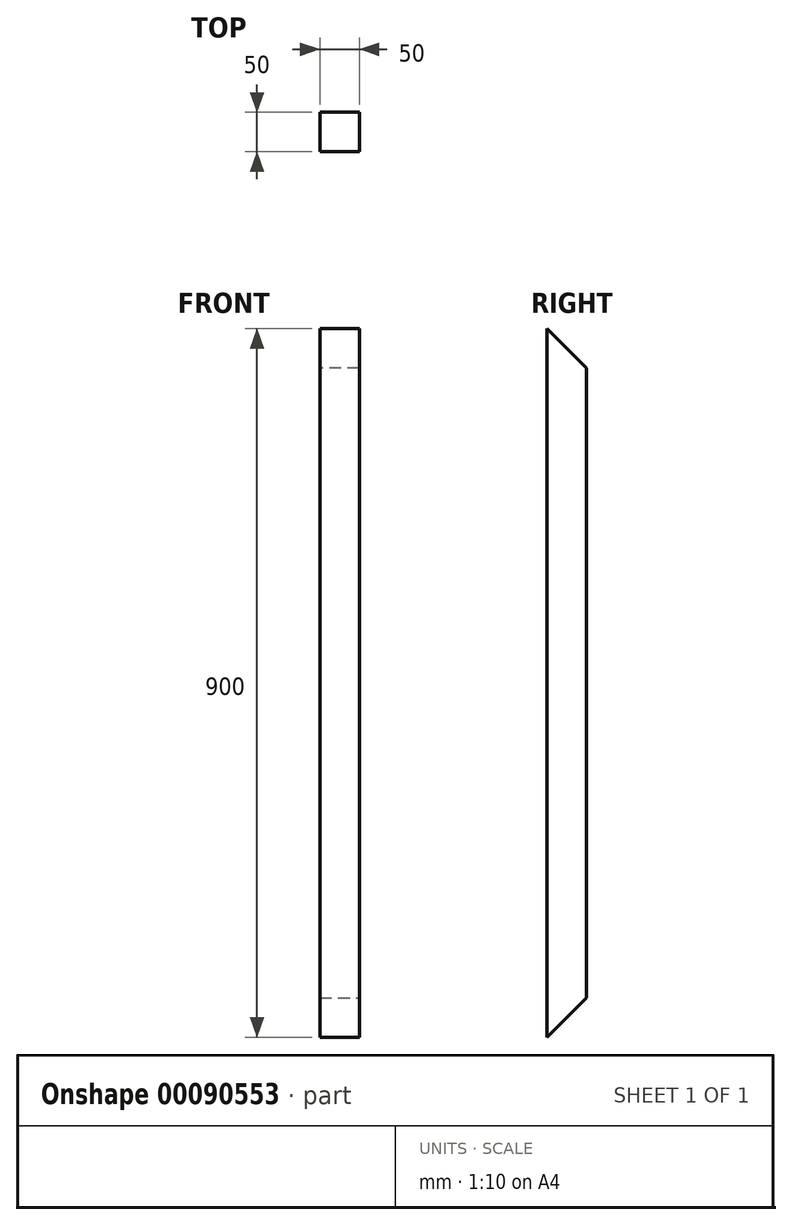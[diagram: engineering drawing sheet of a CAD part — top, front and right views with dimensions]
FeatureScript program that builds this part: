
annotation { "Feature Type Name" : "Feature", "Feature Type Description" : "" }
export const myFeature = defineFeature(function(context is Context, id is Id, definition is map)
    precondition{}
    {
        {
            var Q0;
            Q0=qCreatedBy(makeId("Top.planeOp"),FACE);
            var sketch = newSketch(context, id + "F0", { "sketchPlane" : qUnion([Q0])});
            skLineSegment(sketch, "E0.bottom", {"start": v(25, -25) * mm, "end": v(-25, -25) * mm});
            skLineSegment(sketch, "E0.top", {"start": v(25, 25) * mm, "end": v(-25, 25) * mm});
            skLineSegment(sketch, "E0.left", {"start": v(25, -25) * mm, "end": v(25, 25) * mm});
            skLineSegment(sketch, "E0.right", {"start": v(-25, -25) * mm, "end": v(-25, 25) * mm});
            skPoint(sketch, "E0.middle", {"position": v(0, 0) * mm});
            skSolve(sketch);
        }
        {
            var Q0;
            Q0=qSketchRegion(id+"F0",true);
            extrude(context, id + "F1", {"entities" : qUnion([Q0]), "depth" : 900 * mm});
        }
        {
            var Q0;
            Q0=qCreatedBy(makeId("Right.planeOp"),FACE);
            var sketch = newSketch(context, id + "F2", { "sketchPlane" : qUnion([Q0])});
            skLineSegment(sketch, "E1", {"start": v(-25, 900) * mm, "end": v(135.3, 900) * mm});
            skLineSegment(sketch, "E2", {"start": v(135.3, 900) * mm, "end": v(135.3, 739.7) * mm});
            skLineSegment(sketch, "E3", {"start": v(135.3, 739.7) * mm, "end": v(-25, 900) * mm});
            skSolve(sketch);
        }
        {
            var Q0;
            Q0=qSketchRegion(id+"F2",true);
            extrude(context, id + "F3", {"entities" : qUnion([Q0]), "operationType" : NewBodyOperationType.REMOVE, "endBound" : BoundingType.THROUGH_ALL, "oppositeDirection" : true, "depth" : 25 * mm, "hasSecondDirection" : true, "secondDirectionBound" : SecondDirectionBoundingType.THROUGH_ALL, "secondDirectionOppositeDirection" : false, "secondDirectionDepth" : 25 * mm});
        }
        {
            var Q0;
            Q0=qCreatedBy(makeId("Right.planeOp"),FACE);
            var sketch = newSketch(context, id + "F4", { "sketchPlane" : qUnion([Q0])});
            skLineSegment(sketch, "E4", {"start": v(-25, 0) * mm, "end": v(25, 50) * mm});
            skLineSegment(sketch, "E5", {"start": v(-25, 0) * mm, "end": v(25, 0) * mm});
            skLineSegment(sketch, "E6", {"start": v(25, 50) * mm, "end": v(25, 0) * mm});
            skSolve(sketch);
        }
        {
            var Q0;
            Q0 = qSketchRegion(id + "F4", true);
            extrude(context, id + "F5", {"entities" : qUnion([Q0]), "operationType" : NewBodyOperationType.REMOVE, "endBound" : BoundingType.THROUGH_ALL, "oppositeDirection" : true, "depth" : 25 * mm, "hasSecondDirection" : true, "secondDirectionBound" : SecondDirectionBoundingType.THROUGH_ALL, "secondDirectionOppositeDirection" : false, "secondDirectionDepth" : 25 * mm});
        }
    });
